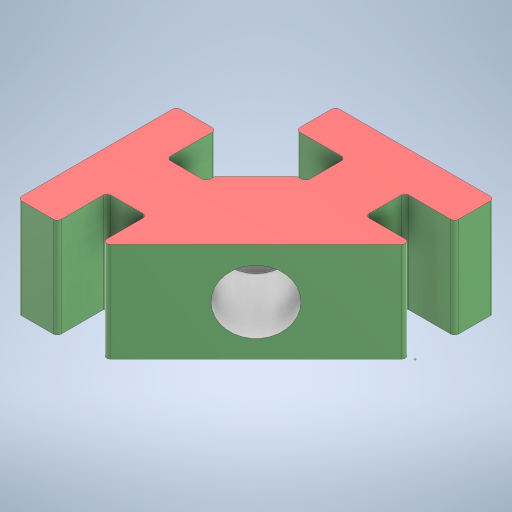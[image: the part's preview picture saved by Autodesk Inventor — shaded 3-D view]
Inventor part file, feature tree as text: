
AUTODESK INVENTOR PART (.ipt)
format: ipt  version: 2023 (Build 270158000, 158)  size: 329,728 bytes
history: native  units: in
note: dims shown in document units (in); Inventor stores cm internally (conversion verified against a paired STEP export)
features: other x5, sketch x3, extrude x3, projected_geometry x2
ambient origin geometry x8: Origin, YZ Plane, XZ Plane, XY Plane, X Axis, Y Axis, Z Axis, Center Point
bodies: Body1 (feature_tree)
feature tree (13):
  other  "FlexPart.ipt"
  sketch  "Sketch1"  dims[d0=0.3937in d1=0.126in]
  other  "Work Point1"
  extrude  "Extrusion1"  Depth=0.3937in
  extrude  "Extrusion2"  Depth=0.0079in
  extrude  "Extrusion3"  Depth=0.0079in
  other  "PLA2::FlexPart.ipt"
  other  "TaggingFeature1"
  projected_geometry  "Projected Loop1"
  sketch  "Sketch2"  dims[d2=0.1575in d3=0.0in d4=0.0079in]
  sketch  "Sketch3"  dims[d5=0.0787in d6=0.0in d7=0.0079in d8=0.0984in d9=0.0in]
  projected_geometry  "Projected Loop2"
  other  "PLA2"
